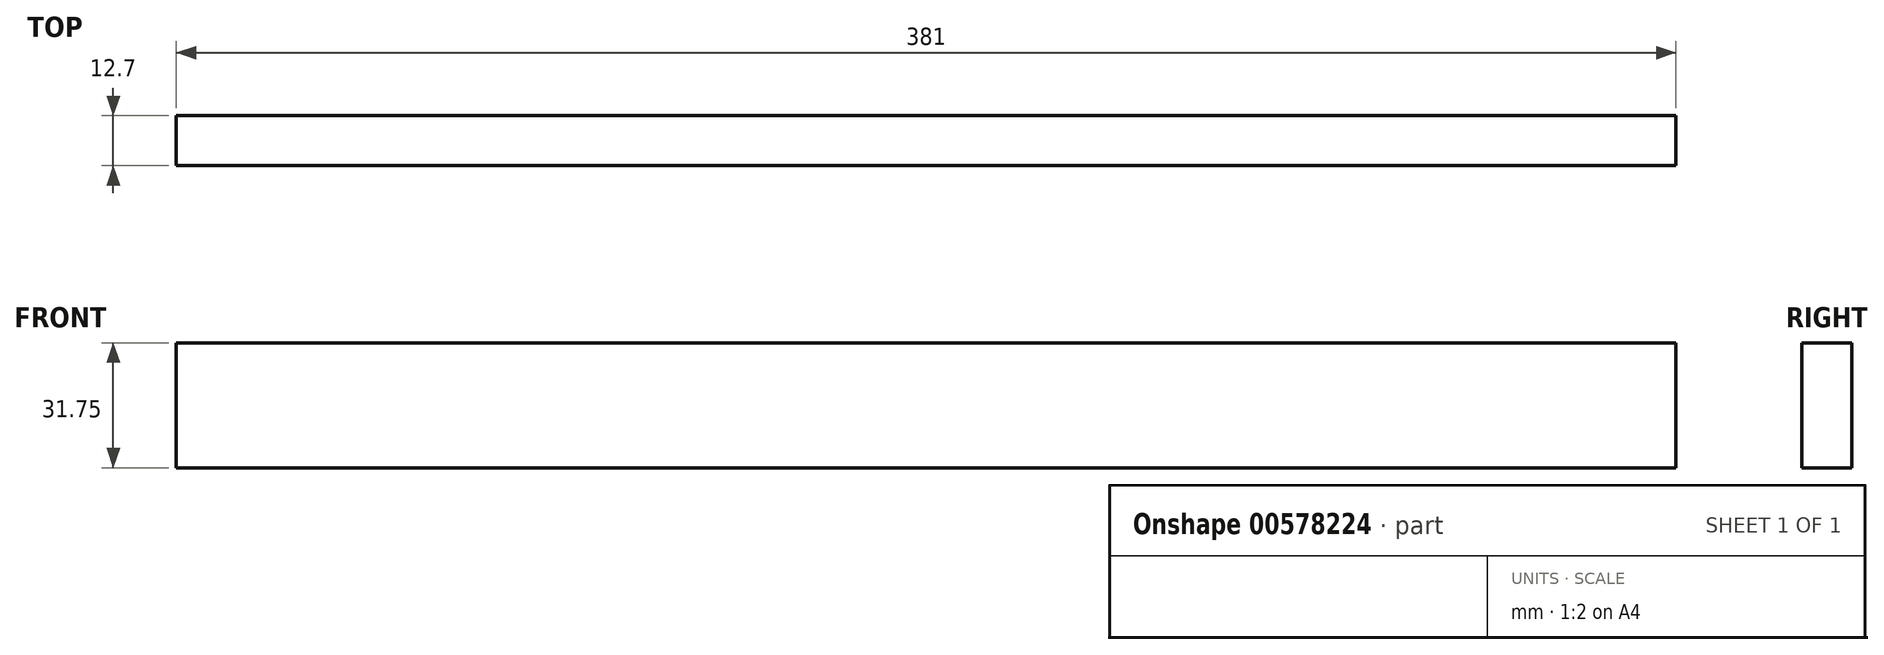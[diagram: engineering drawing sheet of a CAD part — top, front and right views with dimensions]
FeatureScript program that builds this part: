
annotation { "Feature Type Name" : "Feature", "Feature Type Description" : "" }
export const myFeature = defineFeature(function(context is Context, id is Id, definition is map)
    precondition{}
    {
        {
            var Q0;
            Q0=qCreatedBy(makeId("Front.planeOp"),FACE);
            var sketch = newSketch(context, id + "F0", { "sketchPlane" : qUnion([Q0])});
            skLineSegment(sketch, "E0.bottom", {"start": v(-37.14, 15.21) * mm, "end": v(343.86, 15.21) * mm});
            skLineSegment(sketch, "E0.top", {"start": v(-37.14, -16.54) * mm, "end": v(343.86, -16.54) * mm});
            skLineSegment(sketch, "E0.left", {"start": v(-37.14, 15.21) * mm, "end": v(-37.14, -16.54) * mm});
            skLineSegment(sketch, "E0.right", {"start": v(343.86, 15.21) * mm, "end": v(343.86, -16.54) * mm});
            skSolve(sketch);
        }
        {
            var Q0;
            Q0 = qSketchRegion(id + "F0", true);
            extrude(context, id + "F1", {"entities" : qUnion([Q0]), "depth" : 12.7 * mm, "offsetDistance" : 25.4 * mm});
        }
    });
